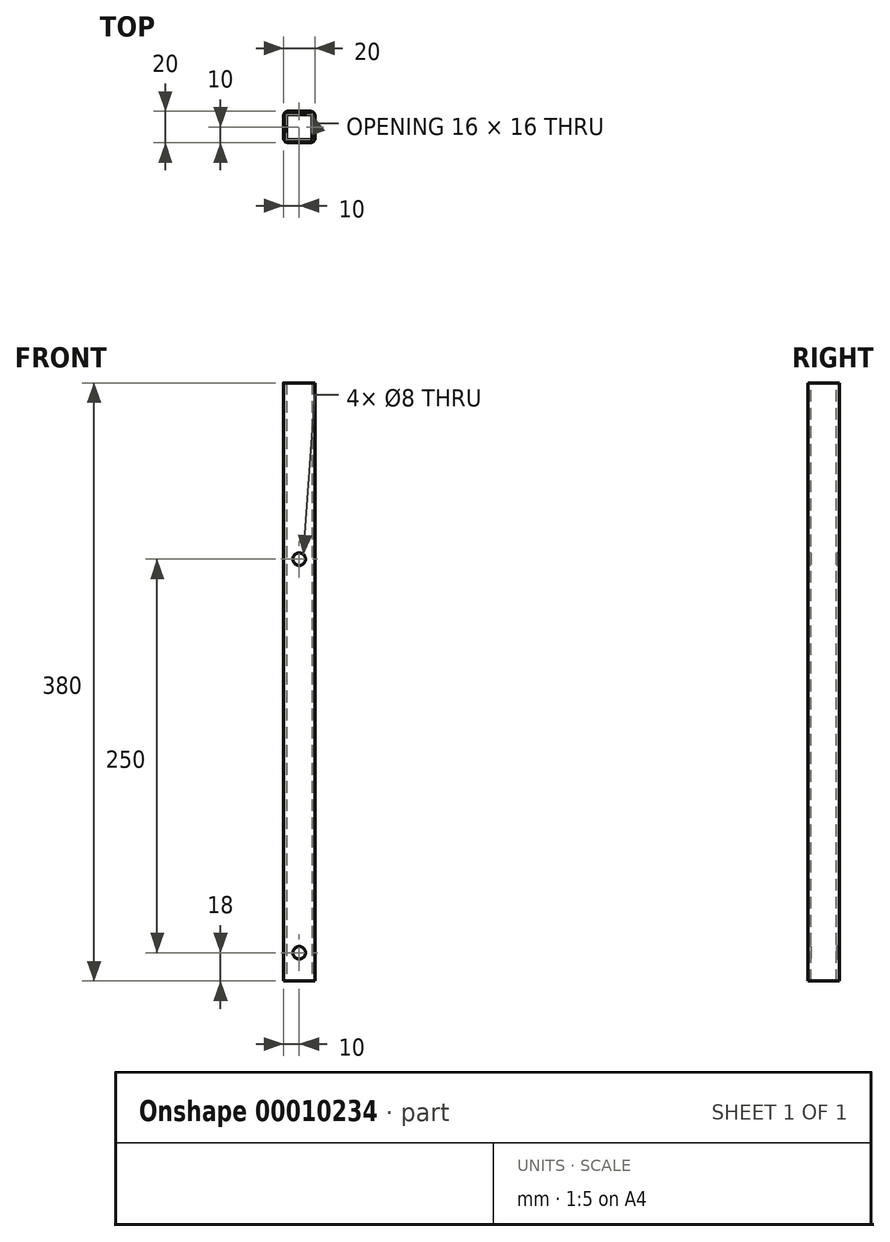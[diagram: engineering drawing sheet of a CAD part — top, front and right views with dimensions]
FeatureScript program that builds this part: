
annotation { "Feature Type Name" : "Feature", "Feature Type Description" : "" }
export const myFeature = defineFeature(function(context is Context, id is Id, definition is map)
    precondition{}
    {
        {
            var Q0;
            Q0=qCreatedBy(makeId("Top.planeOp"),FACE);
            var sketch = newSketch(context, id + "F0", { "sketchPlane" : qUnion([Q0])});
            skLineSegment(sketch, "E0.bottom", {"start": v(-10, 10) * mm, "end": v(10, 10) * mm});
            skLineSegment(sketch, "E0.top", {"start": v(-10, -10) * mm, "end": v(10, -10) * mm});
            skLineSegment(sketch, "E0.left", {"start": v(-10, 10) * mm, "end": v(-10, -10) * mm});
            skLineSegment(sketch, "E0.right", {"start": v(10, 10) * mm, "end": v(10, -10) * mm});
            skSolve(sketch);
        }
        {
            var Q0;
            Q0=makeQuery(id+"F0.imprint","IMPRINT",FACE,{"disambiguationData":[TD([[makeQuery(id+"F0.imprint","IMPRINT",EDGE,{"derivedFrom":sQuery(id+"F0.wireOp",EDGE,"E0.bottom")}),-1.0]])]});
            extrude(context, id + "F1", {"entities" : qUnion([Q0]), "depth" : 380 * mm});
        }
        {
            var Q0;
            Q0=makeQuery(id+"F1.opExtrude","SWEPT_EDGE",EDGE,{"disambiguationData":[OSD([sQuery(id+"F0.wireOp",EDGE,"E0.bottom"),sQuery(id+"F0.wireOp",EDGE,"E0.right")])]});
            var Q1;
            Q1=makeQuery(id+"F1.opExtrude","SWEPT_EDGE",EDGE,{"disambiguationData":[OSD([sQuery(id+"F0.wireOp",EDGE,"E0.top"),sQuery(id+"F0.wireOp",EDGE,"E0.right")])]});
            var Q2;
            Q2=makeQuery(id+"F1.opExtrude","SWEPT_EDGE",EDGE,{"disambiguationData":[OSD([sQuery(id+"F0.wireOp",EDGE,"E0.bottom"),sQuery(id+"F0.wireOp",EDGE,"E0.left")])]});
            var Q3;
            Q3=makeQuery(id+"F1.opExtrude","SWEPT_EDGE",EDGE,{"disambiguationData":[OSD([sQuery(id+"F0.wireOp",EDGE,"E0.top"),sQuery(id+"F0.wireOp",EDGE,"E0.left")])]});
            fillet(context, id + "F2", {"entities" : qUnion([Q0, Q1, Q2, Q3]), "radius" : 3 * mm, "tangentPropagation" : true, "allowEdgeOverflow" : false});
        }
        {
            var Q0;
            Q0=makeQuery(id+"F1.opExtrude","CAP_FACE",FACE,{"disambiguationData":[OSD([sQuery(id+"F0.wireOp",EDGE,"E0.bottom"),sQuery(id+"F0.wireOp",EDGE,"E0.top"),sQuery(id+"F0.wireOp",EDGE,"E0.left"),sQuery(id+"F0.wireOp",EDGE,"E0.right")])],"isStart":false});
            var Q1;
            Q1=makeQuery(id+"F1.opExtrude","CAP_FACE",FACE,{"disambiguationData":[OSD([sQuery(id+"F0.wireOp",EDGE,"E0.bottom"),sQuery(id+"F0.wireOp",EDGE,"E0.top"),sQuery(id+"F0.wireOp",EDGE,"E0.left"),sQuery(id+"F0.wireOp",EDGE,"E0.right")])],"isStart":true});
            shell(context, id + "F3", {"entities" : qUnion([Q0, Q1]), "thickness" : 2 * mm});
        }
        {
            var Q0;
            Q0=makeQuery(id+"F1.opExtrude","SWEPT_FACE",FACE,{"disambiguationData":[OSD([sQuery(id+"F0.wireOp",EDGE,"E0.top")])]});
            var sketch = newSketch(context, id + "F4", { "sketchPlane" : qUnion([Q0])});
            skPoint(sketch, "E1", {"position": v(0, 18) * mm});
            skPoint(sketch, "E2", {"position": v(0, 268) * mm});
            skSolve(sketch);
        }
        {
            var Q0;
            Q0=sQuery(id+"F4.wireOp",VERTEX,"E1");
            var Q1;
            Q1=makeQuery(id+"F1.opExtrude","SWEPT_BODY",BODY,{"disambiguationData":[OSD([sQuery(id+"F0.wireOp",EDGE,"E0.bottom"),sQuery(id+"F0.wireOp",EDGE,"E0.top"),sQuery(id+"F0.wireOp",EDGE,"E0.left"),sQuery(id+"F0.wireOp",EDGE,"E0.right")])]});
            hole(context, id + "F5", {"style" : HoleStyle.SIMPLE, "holeDiameter" : 8 * mm, "endStyle" : HoleEndStyle.THROUGH, "locations" : qUnion([Q0]), "scope" : qUnion([Q1])});
        }
        {
            var Q0;
            Q0=sQuery(id+"F4.wireOp",VERTEX,"E2");
            var Q1;
            Q1=makeQuery(id+"F1.opExtrude","SWEPT_BODY",BODY,{"disambiguationData":[OSD([sQuery(id+"F0.wireOp",EDGE,"E0.bottom"),sQuery(id+"F0.wireOp",EDGE,"E0.top"),sQuery(id+"F0.wireOp",EDGE,"E0.left"),sQuery(id+"F0.wireOp",EDGE,"E0.right")])]});
            hole(context, id + "F6", {"style" : HoleStyle.SIMPLE, "holeDiameter" : 8 * mm, "endStyle" : HoleEndStyle.THROUGH, "locations" : qUnion([Q0]), "scope" : qUnion([Q1])});
        }
    });
